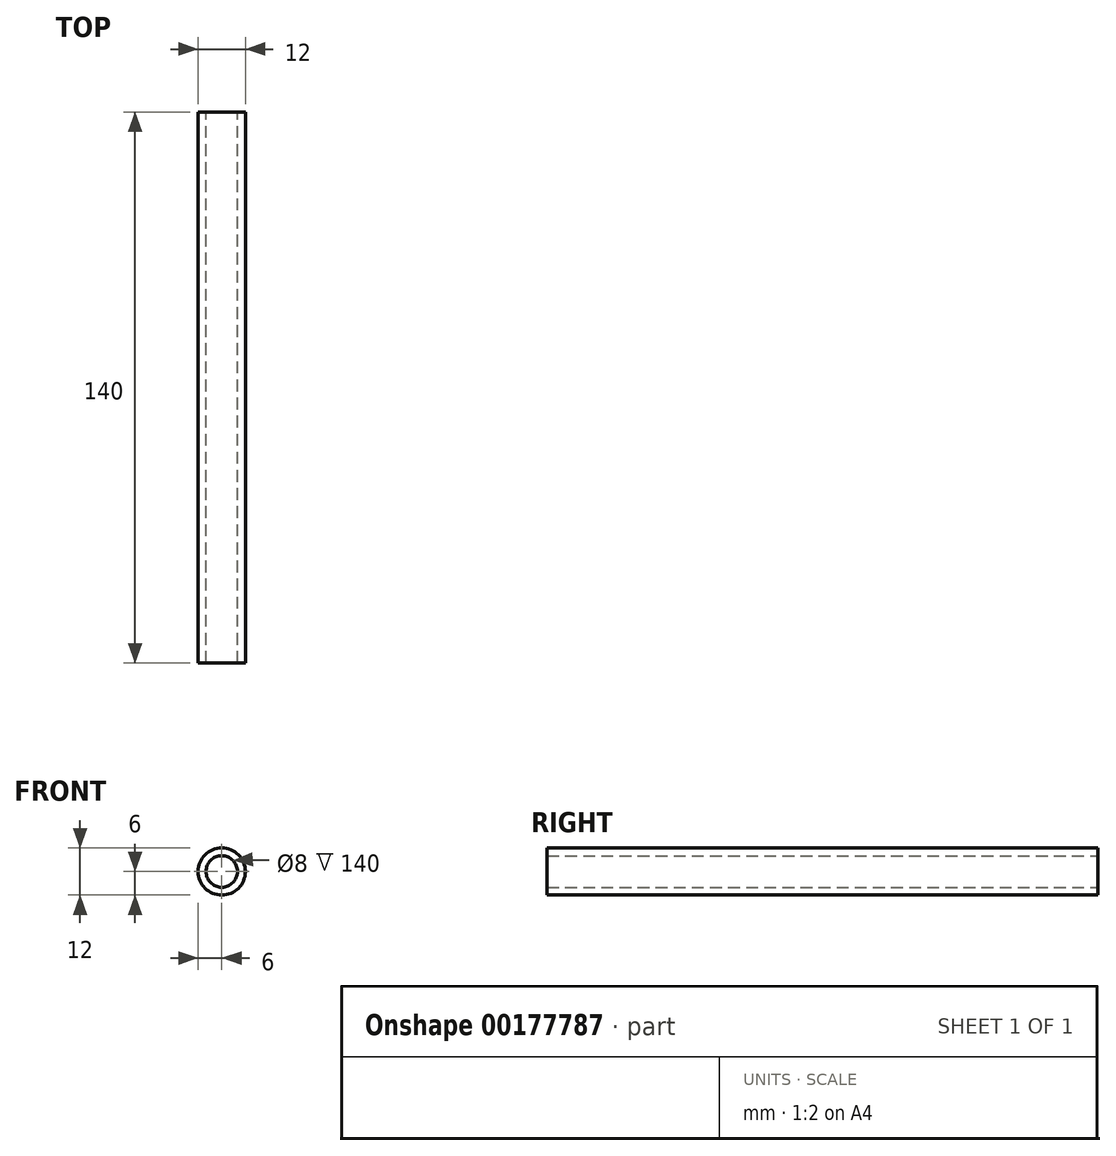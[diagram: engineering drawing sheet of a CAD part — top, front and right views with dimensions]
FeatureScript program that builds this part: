
annotation { "Feature Type Name" : "Feature", "Feature Type Description" : "" }
export const myFeature = defineFeature(function(context is Context, id is Id, definition is map)
    precondition{}
    {
        {
            var Q0;
            Q0=qCreatedBy(makeId("Front.planeOp"),FACE);
            var sketch = newSketch(context, id + "F0", { "sketchPlane" : qUnion([Q0])});
            skCircle(sketch, "E0", {"center": v(0, 0) * mm, "radius": 6 * mm});
            skCircle(sketch, "E1", {"center": v(0, 0) * mm, "radius": 4 * mm});
            skSolve(sketch);
        }
        {
            var Q0;
            Q0=qSketchRegion(id+"F0",true);
            extrude(context, id + "F1", {"entities" : qUnion([Q0]), "endBound" : BoundingType.SYMMETRIC, "depth" : 140 * mm});
        }
    });
